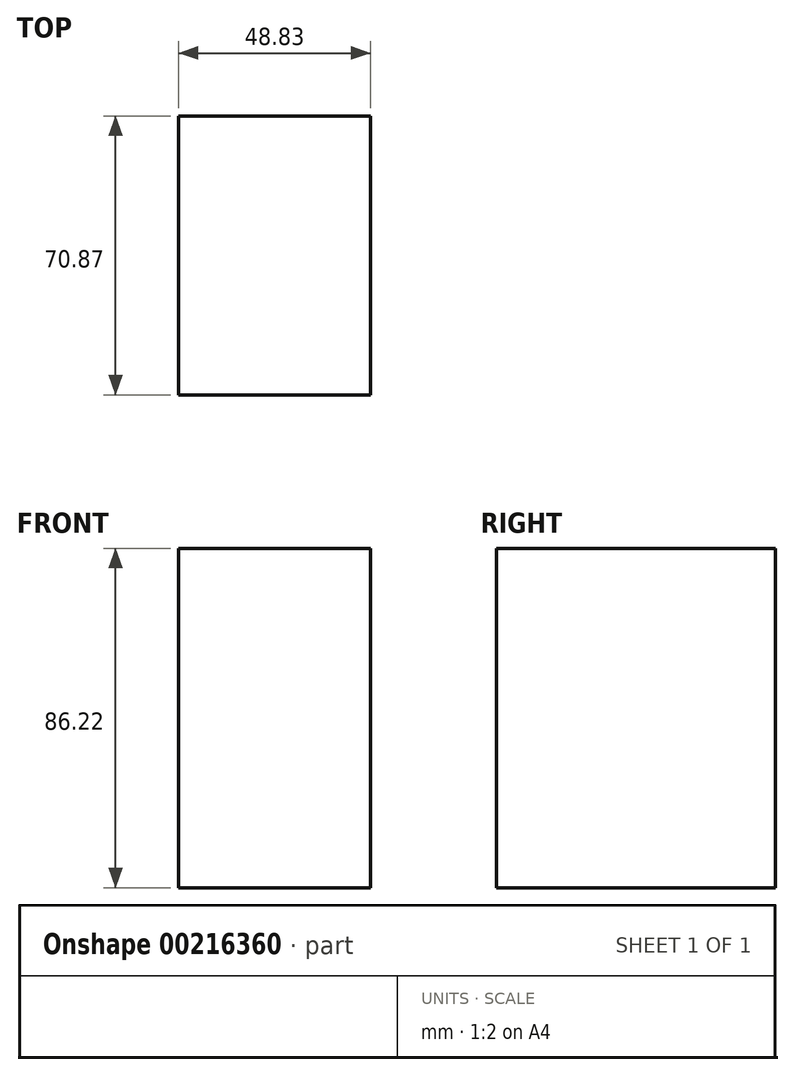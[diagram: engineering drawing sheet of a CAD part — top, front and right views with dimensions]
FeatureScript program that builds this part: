
annotation { "Feature Type Name" : "Feature", "Feature Type Description" : "" }
export const myFeature = defineFeature(function(context is Context, id is Id, definition is map)
    precondition{}
    {
        {
            var Q0;
            Q0=qCreatedBy(makeId("Front.planeOp"),FACE);
            var sketch = newSketch(context, id + "F0", { "sketchPlane" : qUnion([Q0])});
            skLineSegment(sketch, "E0.bottom", {"start": v(0, -49.97) * mm, "end": v(-48.83, -49.97) * mm});
            skLineSegment(sketch, "E0.top", {"start": v(0, 36.25) * mm, "end": v(-48.83, 36.25) * mm});
            skLineSegment(sketch, "E0.left", {"start": v(0, -49.97) * mm, "end": v(0, 36.25) * mm});
            skLineSegment(sketch, "E0.right", {"start": v(-48.83, -49.97) * mm, "end": v(-48.83, 36.25) * mm});
            skSolve(sketch);
        }
        {
            var Q0;
            Q0=makeQuery(id+"F0.imprint","IMPRINT",FACE,{"disambiguationData":[TD([[makeQuery(id+"F0.imprint","IMPRINT",EDGE,{"derivedFrom":sQuery(id+"F0.wireOp",EDGE,"E0.bottom")}),-1.0]])]});
            extrude(context, id + "F1", {"entities" : qUnion([Q0]), "depth" : 70.87 * mm});
        }
    });
